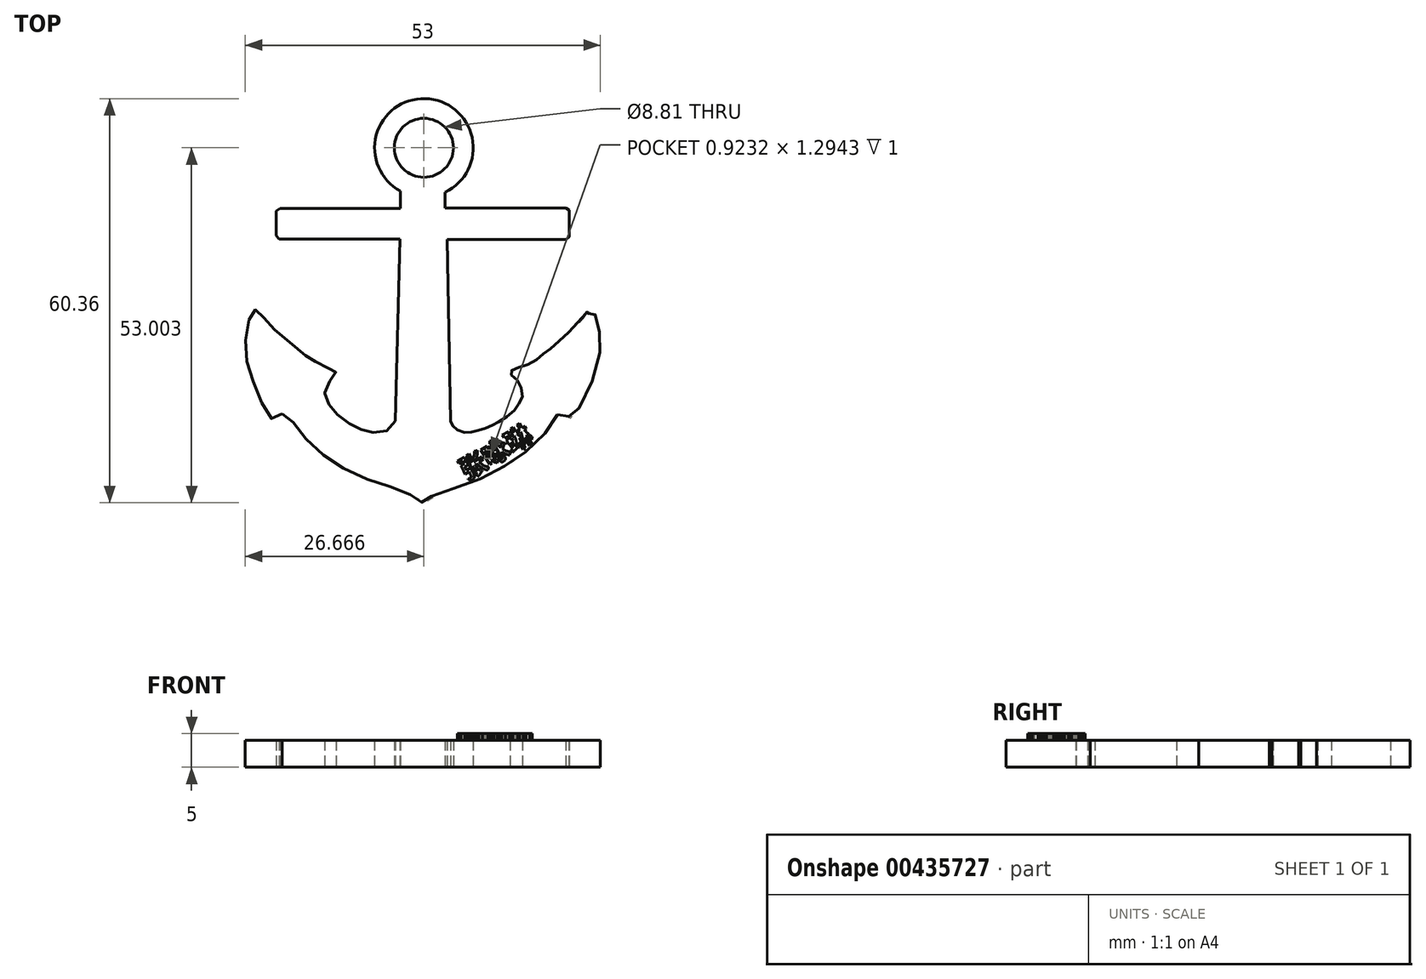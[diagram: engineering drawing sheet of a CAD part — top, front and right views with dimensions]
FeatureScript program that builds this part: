
annotation { "Feature Type Name" : "Feature", "Feature Type Description" : "" }
export const myFeature = defineFeature(function(context is Context, id is Id, definition is map)
    precondition{}
    {
        {
            var Q0;
            Q0=qCreatedBy(makeId("Top.planeOp"),FACE);
            var sketch = newSketch(context, id + "F0", { "sketchPlane" : qUnion([Q0])});
            skLineSegment(sketch, "E0", {"start": v(-3.3, 13.86) * mm, "end": v(-3.3, 11.3) * mm});
            skLineSegment(sketch, "E1", {"start": v(-3.3, 11.3) * mm, "end": v(-21.24, 11.3) * mm});
            skLineSegment(sketch, "E2", {"start": v(-21.8, 10.89) * mm, "end": v(-21.8, 7.19) * mm});
            skLineSegment(sketch, "E3", {"start": v(-21.38, 6.66) * mm, "end": v(-3.36, 6.66) * mm});
            skLineSegment(sketch, "E4", {"start": v(-3.36, 6.66) * mm, "end": v(-4.07, -20.48) * mm});
            skLineSegment(sketch, "E5", {"start": v(3.42, 13.68) * mm, "end": v(3.42, 11.35) * mm});
            skLineSegment(sketch, "E6", {"start": v(3.42, 11.35) * mm, "end": v(21.44, 11.35) * mm});
            skLineSegment(sketch, "E7", {"start": v(21.91, 11.01) * mm, "end": v(21.91, 7.03) * mm});
            skLineSegment(sketch, "E8", {"start": v(21.45, 6.62) * mm, "end": v(3.7, 6.62) * mm});
            skLineSegment(sketch, "E9", {"start": v(3.7, 6.62) * mm, "end": v(4.24, -20.49) * mm});
            skArc(sketch, "E10", {"start": v(3.42, 13.68) * mm, "mid": v(0.43, 27.67) * mm, "end": v(-3.3, 13.86) * mm});
            skCircle(sketch, "E11", {"center": v(0.24, 20.31) * mm, "radius": 4.4 * mm});
            skFitSpline(sketch, "E12", {"points": [v(-4.07, -20.48) * mm, v(-5.23, -21.92) * mm, v(-7.33, -22.22) * mm, v(-8.94, -21.8) * mm, v(-10.65, -21.04) * mm, v(-12.64, -19.57) * mm, v(-13.86, -18.1) * mm, v(-14.53, -16.57) * mm, v(-14.1, -14.79) * mm, v(-12.85, -13.53) * mm, v(-13.35, -12.77) * mm, v(-14.07, -12.62) * mm, v(-16.17, -11.5) * mm, v(-17.32, -10.77) * mm, v(-20.98, -7.77) * mm, v(-23.18, -5.64) * mm, v(-24.65, -3.93) * mm, v(-25.17, -4.03) * mm, v(-26.22, -6.79) * mm, v(-26.15, -11.82) * mm, v(-24.4, -16.64) * mm, v(-22.38, -20.2) * mm, v(-20.91, -19.43) * mm], "startDerivative": vector(-22.58, -39.92) * mm, "endDerivative": vector(38.05, 35.16) * mm});
            skFitSpline(sketch, "E13", {"points": [v(-20.91, -19.43) * mm, v(-20.4, -19.43) * mm, v(-19.5, -20.37) * mm, v(-18.92, -21.35) * mm, v(-17.3, -23.24) * mm, v(-15.23, -25.17) * mm, v(-13.73, -26.33) * mm, v(-10.94, -27.99) * mm, v(-8.16, -29.23) * mm, v(-5.67, -30.06) * mm, v(-3.6, -30.73) * mm, v(-1.62, -31.58) * mm, v(-0.68, -32.02) * mm, v(-0.22, -32.58) * mm, v(0.51, -32.63) * mm, v(0.82, -32.27) * mm, v(1.56, -31.6) * mm, v(3.5, -30.9) * mm, v(7.24, -29.65) * mm, v(10.22, -28.4) * mm, v(13.3, -26.59) * mm, v(15.45, -25.03) * mm, v(17.88, -22.78) * mm, v(19.78, -20.34) * mm, v(20.32, -19.43) * mm, v(21, -19.43) * mm, v(21.68, -19.63) * mm, v(22.27, -20.08) * mm, v(22.95, -19.43) * mm, v(24.17, -17.02) * mm, v(26.1, -12.43) * mm, v(26.56, -9.56) * mm, v(26.52, -7.78) * mm, v(26.21, -5.94) * mm, v(25.86, -4.7) * mm, v(25.35, -4.02) * mm, v(24.89, -3.9) * mm, v(24.09, -4.86) * mm, v(21.84, -7.2) * mm], "startDerivative": vector(35.42, 8.92) * mm, "endDerivative": vector(-41.35, -28.75) * mm});
            skFitSpline(sketch, "E14", {"points": [v(21.84, -7.2) * mm, v(19.45, -9.43) * mm, v(18.06, -10.5) * mm, v(16.71, -11.53) * mm, v(14.9, -12.35) * mm, v(13.53, -12.77) * mm, v(13.11, -13.36) * mm, v(13.73, -13.92) * mm, v(14.55, -15.04) * mm, v(14.97, -16.66) * mm, v(14.41, -17.92) * mm, v(13.69, -18.94) * mm, v(12.03, -20.24) * mm, v(10.86, -20.9) * mm, v(9.89, -21.4) * mm, v(8.78, -21.78) * mm, v(7.8, -22.05) * mm, v(6.8, -22.18) * mm, v(5.78, -22.07) * mm, v(4.76, -21.5) * mm, v(4.4, -20.97) * mm, v(4.24, -20.49) * mm], "startDerivative": vector(-33.36, -32.74) * mm, "endDerivative": vector(-4.47, 16.17) * mm});
            skFitSpline(sketch, "E15", {"points": [v(21.44, 11.35) * mm, v(21.91, 11.01) * mm], "startDerivative": vector(0.47, -0.34) * mm, "endDerivative": vector(0.47, -0.34) * mm});
            skFitSpline(sketch, "E16", {"points": [v(21.91, 7.03) * mm, v(21.45, 6.62) * mm], "startDerivative": vector(-0.46, -0.41) * mm, "endDerivative": vector(-0.46, -0.41) * mm});
            skFitSpline(sketch, "E17", {"points": [v(-21.8, 7.19) * mm, v(-21.38, 6.66) * mm], "startDerivative": vector(0.42, -0.52) * mm, "endDerivative": vector(0.42, -0.52) * mm});
            skFitSpline(sketch, "E18", {"points": [v(-21.24, 11.3) * mm, v(-21.8, 10.89) * mm], "startDerivative": vector(-0.56, -0.4) * mm, "endDerivative": vector(-0.56, -0.4) * mm});
            skSolve(sketch);
        }
        {
            var Q0;
            Q0=makeQuery(id+"F0.imprint","IMPRINT",FACE,{"disambiguationData":[TD([[makeQuery(id+"F0.imprint","IMPRINT",EDGE,{"derivedFrom":sQuery(id+"F0.wireOp",EDGE,"E0")}),1.0]])]});
            extrude(context, id + "F1", {"entities" : qUnion([Q0]), "depth" : 4 * mm});
        }
        {
            var Q0;
            Q0=qCreatedBy(makeId("Top.planeOp"),FACE);
            var sketch = newSketch(context, id + "F2", { "sketchPlane" : qUnion([Q0])});
            skText(sketch, "E19", { "text": "张咏琳", "fontName": "NotoSansCJKsc-Bold.otf"});
            const initialGuessF2  = {"E19": [0.00662, -0.0294, 0.85866, 0.51255, 0.00284]};
            skSetInitialGuess(sketch, initialGuessF2);
            skSolve(sketch);
        }
        {
            var Q0;
            Q0 = qSketchRegion(id + "F2", true);
            extrude(context, id + "F3", {"entities" : qUnion([Q0]), "operationType" : NewBodyOperationType.ADD, "depth" : 5 * mm});
        }
    });
